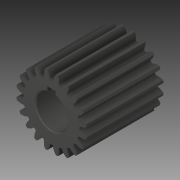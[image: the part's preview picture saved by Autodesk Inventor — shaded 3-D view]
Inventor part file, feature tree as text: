
AUTODESK INVENTOR PART (.ipt)
format: ipt  version: 2019 (Build 230136000, 136)  size: 299,008 bytes
history: native  units: in
note: dims shown in document units (in); Inventor stores cm internally (conversion verified against a paired STEP export)
features: chamfer x1
ambient origin geometry x8: Origin, YZ Plane, XZ Plane, XY Plane, X Axis, Y Axis, Z Axis, Center Point
bodies: Solid1 (feature_tree)
feature tree (1):
  chamfer  "Chamfer1"  [1 undecoded]
note: 1 required parameter value undecoded (feature->parameter linkage not recoverable at this tier; creation-order binding heuristic only, values carry confidence <= 0.55)
